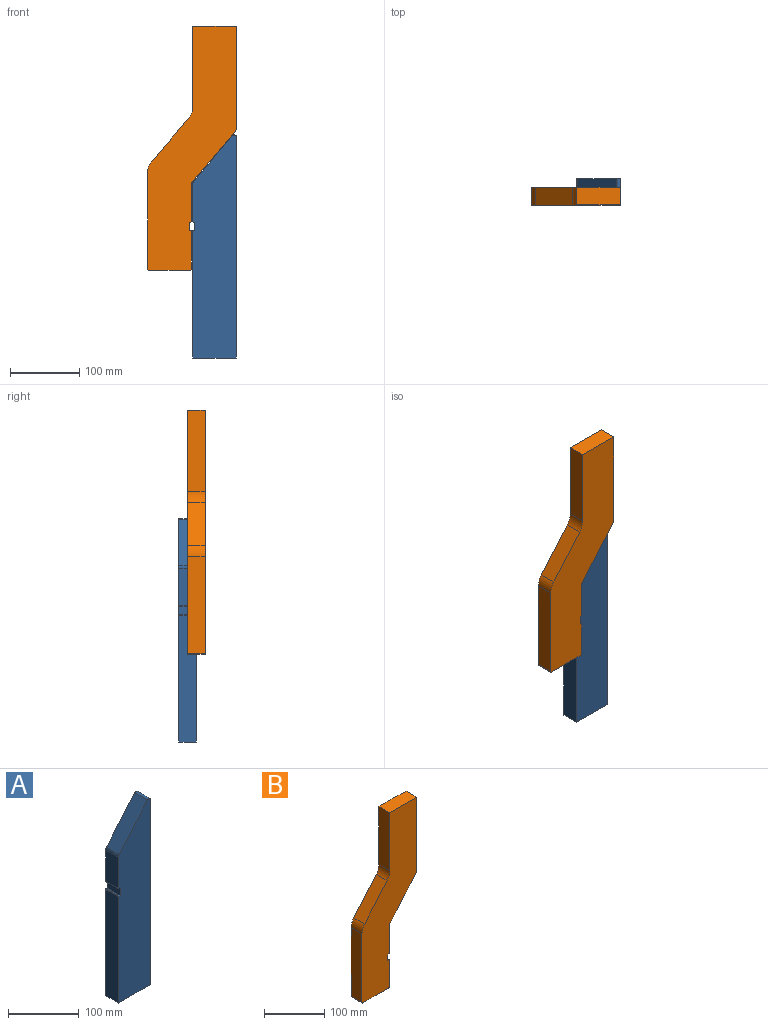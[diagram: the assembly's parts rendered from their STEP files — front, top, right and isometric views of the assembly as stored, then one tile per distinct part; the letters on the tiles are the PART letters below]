
ASSEMBLY  parts=2 mates=2
PART A: 14 faces, bbox 63.5x25.4x322.9 mm
  f0: plane 63.5x25.4mm, normal (0,0,-1), area 1612.9mm2, adj f1,f7,f8,f9
  f1: plane 319.74x25.4mm, normal (1,0,0), area 8121.3mm2, adj f0,f8,f9,f10
  f2: plane 66.02x56.39mm, normal (-0.76,0,0.65), area 2205.3mm2, adj f8,f9,f10,f11
  f3: plane 54.01x25.4mm, normal (-1,0,0), area 1371.9mm2, adj f8,f9,f11,f12
  f4: plane 25.4x2.38mm, normal (0,0,-1), area 60.5mm2, adj f5,f8,f9,f12
  f5: plane 25.4x12.7mm, normal (-1,0,0), area 322.6mm2, adj f4,f6,f8,f9
  f6: plane 25.4x2.38mm, normal (0,0,1), area 60.5mm2, adj f5,f8,f9,f13
  f7: plane 183.36x25.4mm, normal (-1,0,0), area 4657.2mm2, adj f0,f8,f9,f13
  f8: plane 322.91x63.5mm, normal (0,-1,0), area 18433.1mm2, adj f0,f1,f2,f3,f4,f5,f6,f7
  f9: plane 322.91x63.5mm, normal (0,1,0), area 18433.1mm2, adj f0,f1,f2,f3,f4,f5,f6,f7
  f10: cylinder r=3.17mm len=25.4mm, axis (0,-1,0), area 196.3mm2, adj f1,f2,f8,f9
  f11: cylinder r=6.35mm len=25.4mm, axis (0,-1,0), area 114mm2, adj f2,f3,f8,f9
  f12: cylinder r=0.79mm len=25.4mm, axis (0,1,0), area 31.7mm2, adj f3,f4,f8,f9
  f13: cylinder r=0.79mm len=25.4mm, axis (0,-1,0), area 31.7mm2, adj f6,f7,f8,f9
PART B: 22 faces, bbox 128.6x25.4x353.6 mm
  f0: plane 54.01x25.4mm, normal (1,0,0), area 1371.9mm2, adj f12,f13,f19,f21
  f1: plane 72.64x62.04mm, normal (0.76,0,-0.65), area 2426.4mm2, adj f12,f13,f16,f19
  f2: plane 148.09x25.4mm, normal (1,0,0), area 3761.4mm2, adj f3,f12,f13,f16
  f3: plane 63.5x25.4mm, normal (0,0,1), area 1612.9mm2, adj f2,f4,f12,f13
  f4: plane 117.63x25.4mm, normal (-1,0,0), area 2987.8mm2, adj f3,f12,f13,f14
  f5: plane 61.95x52.91mm, normal (-0.76,0,0.65), area 2069.4mm2, adj f12,f13,f14,f15
  f6: plane 139.47x25.4mm, normal (-1,0,0), area 3542.5mm2, adj f12,f13,f15,f17
  f7: plane 60.33x25.4mm, normal (0,0,-1), area 1532.3mm2, adj f12,f13,f17,f18
  f8: plane 54.77x25.4mm, normal (1,0,0), area 1391.1mm2, adj f12,f13,f18,f20
  f9: plane 25.4x2.38mm, normal (0,0,1), area 60.5mm2, adj f10,f12,f13,f20
  f10: plane 25.4x12.7mm, normal (1,0,0), area 322.6mm2, adj f9,f11,f12,f13
  f11: plane 25.4x2.38mm, normal (0,0,-1), area 60.5mm2, adj f10,f12,f13,f21
  f12: plane 353.63x128.59mm, normal (0,-1,0), area 23938.6mm2, adj f0,f1,f2,f3,f4,f5,f6,f7
  f13: plane 353.63x128.59mm, normal (0,1,0), area 23938.6mm2, adj f0,f1,f2,f3,f4,f5,f6,f7
  f14: cylinder r=25.4mm len=25.4mm, axis (0,-1,0), area 456.1mm2, adj f4,f5,f12,f13
  f15: cylinder r=25.4mm len=25.4mm, axis (0,1,0), area 456.1mm2, adj f5,f6,f12,f13
  f16: cylinder r=6.35mm len=25.4mm, axis (0,1,0), area 114mm2, adj f1,f2,f12,f13
  f17: cylinder r=1.59mm len=25.4mm, axis (0,-1,0), area 63.3mm2, adj f6,f7,f12,f13
  f18: cylinder r=1.59mm len=25.4mm, axis (0,1,0), area 63.3mm2, adj f7,f8,f12,f13
  f19: cylinder r=6.35mm len=25.4mm, axis (0,-1,0), area 114mm2, adj f0,f1,f12,f13
  f20: cylinder r=0.79mm len=25.4mm, axis (0,-1,0), area 31.7mm2, adj f8,f9,f12,f13
  f21: cylinder r=0.79mm len=25.4mm, axis (0,-1,0), area 31.7mm2, adj f0,f11,f12,f13
PLACE A t=(-8.06,0.31,94.2)mm
PLACE B t=(-8.06,-12.39,94.2)mm
MATE planar B.f11 <-> A.f4  axis (0,0,-1) through (-75.13,-25.09,37.05)mm
MATE planar A.f1 <-> B.f2  axis (1,0,0) through (-8.06,-12.39,0.07)mm
